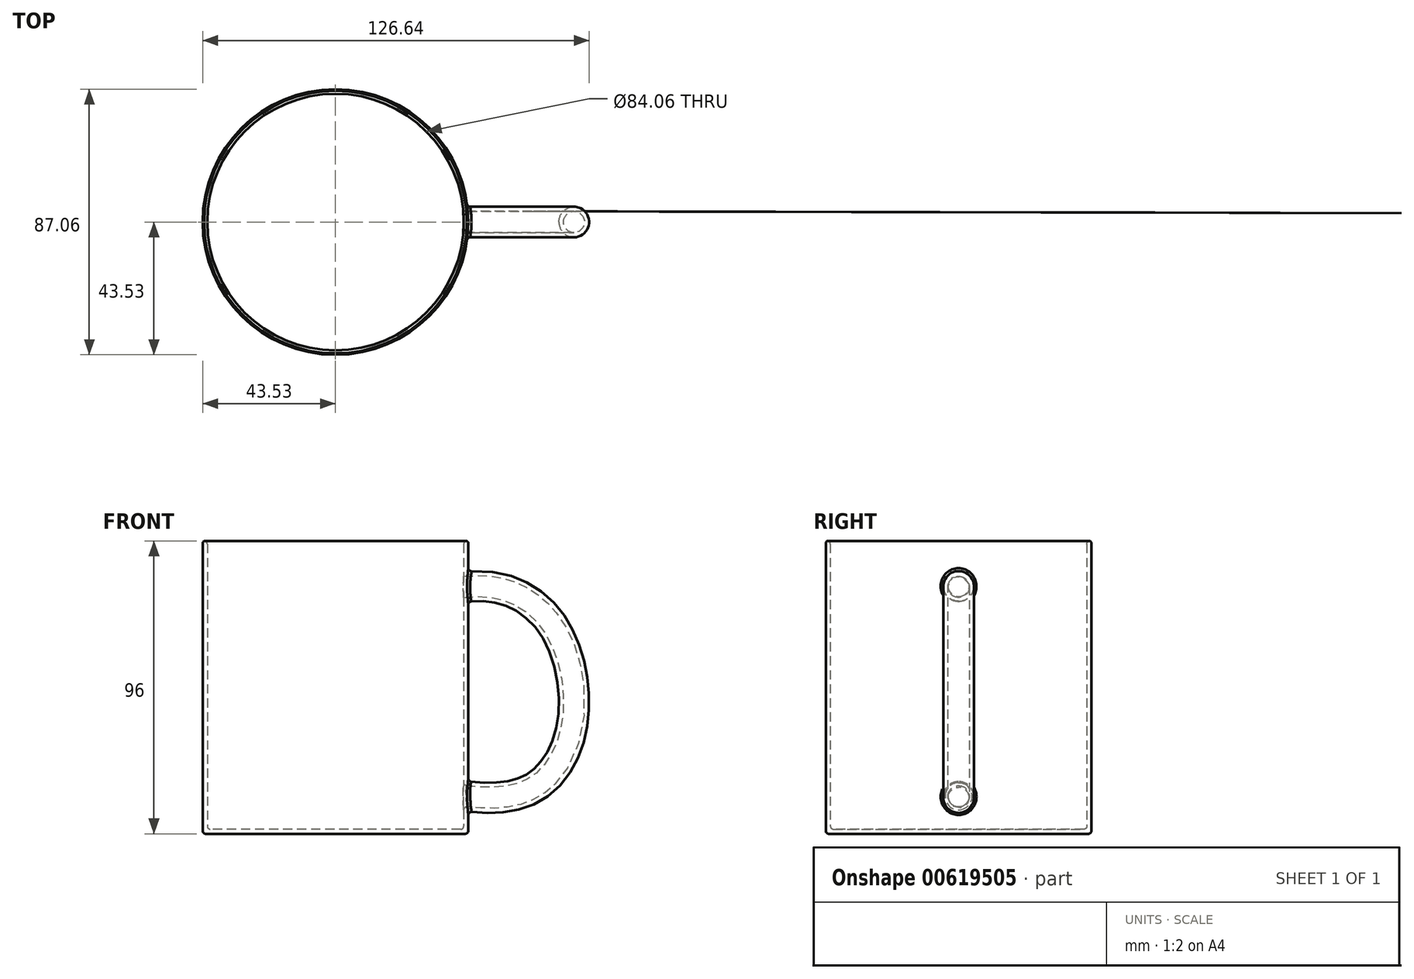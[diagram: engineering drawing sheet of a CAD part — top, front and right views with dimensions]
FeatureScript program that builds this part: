
annotation { "Feature Type Name" : "Feature", "Feature Type Description" : "" }
export const myFeature = defineFeature(function(context is Context, id is Id, definition is map)
    precondition{}
    {
        {
            var Q0;
            Q0=qCreatedBy(makeId("Top.planeOp"),FACE);
            var sketch = newSketch(context, id + "F0", { "sketchPlane" : qUnion([Q0])});
            skCircle(sketch, "E0", {"center": v(0, 0) * mm, "radius": 43.53 * mm});
            skSolve(sketch);
        }
        {
            var Q0;
            Q0 = qSketchRegion(id + "F0", true);
            extrude(context, id + "F1", {"entities" : qUnion([Q0]), "depth" : 96 * mm, "offsetDistance" : 25 * mm});
        }
        {
            var Q0;
            Q0=qCreatedBy(makeId("Front.planeOp"),FACE);
            var sketch = newSketch(context, id + "F2", { "sketchPlane" : qUnion([Q0])});
            skFitSpline(sketch, "E1", {"points": [v(33.38, 80.11) * mm, v(54.68, 80.88) * mm, v(72.35, 67.6) * mm, v(78.42, 37.38) * mm, v(68.76, 17.16) * mm, v(53.58, 11.3) * mm, v(33.56, 13.32) * mm], "startDerivative": vector(134.8, 28.45) * mm, "endDerivative": vector(-122.24, 25.91) * mm});
            skSolve(sketch);
        }
        {
            var Q0;
            Q0=qCreatedBy(makeId("Right.planeOp"),FACE);
            cPlane(context, id + "F3", {"entities" : qUnion([Q0]), "cplaneType" : CPlaneType.OFFSET, "offset" : 38.6 * mm, "width" : 150 * mm, "height" : 150 * mm});
        }
        {
            var Q0;
            Q0=qCreatedBy(id+"F3.planeOp",FACE);
            var sketch = newSketch(context, id + "F4", { "sketchPlane" : qUnion([Q0])});
            skCircle(sketch, "E2", {"center": v(0, 80.47) * mm, "radius": 5 * mm});
            skSolve(sketch);
        }
        {
            var Q0;
            Q0 = qSketchRegion(id + "F4", true);
            var Q1;
            Q1 = qConstructionFilter(qBodyType(qCreatedBy(id + "F2" ,EDGE), BodyType.WIRE), ConstructionObject.NO);
            sweep(context, id + "F5", {"operationType" : NewBodyOperationType.ADD, "profiles" : qUnion([Q0]), "path" : qUnion([Q1])});
        }
        {
            var Q0;
            Q0=makeQuery(id+"F1.opExtrude","CAP_FACE",FACE,{"disambiguationData":[OSD([sQuery(id+"F0.wireOp",EDGE,"E0")])],"isStart":false});
            shell(context, id + "F6", {"entities" : qUnion([Q0]), "thickness" : 1.5 * mm});
        }
        {
            var Q0;
            {var subQ0=sQuery(id+"F0.wireOp",EDGE,"E0");Q0=makeQuery(id+"F6.opShell","OFFSET_EDGE",EDGE,{"disambiguationData":[OSD([subQ0]),TDD([makeQuery(id+"F1.opExtrude","CAP_EDGE",EDGE,{"disambiguationData":[OSD([subQ0])],"isStart":false})])]});}
            fillet(context, id + "F7", {"entities" : qUnion([Q0]), "radius" : 1 * mm, "tangentPropagation" : true, "allowEdgeOverflow" : false});
        }
        {
            var Q0;
            Q0=makeQuery(id+"F1.opExtrude","CAP_EDGE",EDGE,{"disambiguationData":[OSD([sQuery(id+"F0.wireOp",EDGE,"E0")])],"isStart":false});
            fillet(context, id + "F8", {"entities" : qUnion([Q0]), "radius" : 1 * mm, "tangentPropagation" : true, "allowEdgeOverflow" : false});
        }
        {
            var Q0;
            Q0=makeQuery(id+"F1.opExtrude","CAP_FACE",FACE,{"disambiguationData":[OSD([sQuery(id+"F0.wireOp",EDGE,"E0")])],"isStart":true});
            fillet(context, id + "F9", {"entities" : qUnion([Q0]), "radius" : 1 * mm, "tangentPropagation" : true, "allowEdgeOverflow" : false});
        }
        {
            var Q0;
            {var subQ0=sQuery(id+"F0.wireOp",EDGE,"E0");Q0=makeQuery(id+"F6.opShell","OFFSET_EDGE",EDGE,{"disambiguationData":[OSD([subQ0]),TDD([makeQuery(id+"F1.opExtrude","CAP_EDGE",EDGE,{"disambiguationData":[OSD([subQ0])],"isStart":true})])]});}
            fillet(context, id + "F10", {"entities" : qUnion([Q0]), "radius" : 1 * mm, "tangentPropagation" : true, "allowEdgeOverflow" : false});
        }
        {
            var Q0;
            Q0=makeQuery(id+"F5.boolean.opBoolean","INTERSECT",EDGE,{"disambiguationData":[OD(1.0)],"derivedFrom":[makeQuery(id+"F1.opExtrude","SWEPT_FACE",FACE,{"disambiguationData":[OSD([sQuery(id+"F0.wireOp",EDGE,"E0")])]}),makeQuery(id+"F5.opSweep","SWEPT_FACE",FACE,{"disambiguationData":[OSD([sQuery(id+"F2.wireOp",EDGE,"E1"),sQuery(id+"F4.wireOp",EDGE,"E2")])]})]});
            fillet(context, id + "F11", {"entities" : qUnion([Q0]), "radius" : 1 * mm, "tangentPropagation" : true, "allowEdgeOverflow" : false});
        }
        {
            var Q0;
            Q0=makeQuery(id+"F5.boolean.opBoolean","INTERSECT",EDGE,{"disambiguationData":[OD(0.0)],"derivedFrom":[makeQuery(id+"F1.opExtrude","SWEPT_FACE",FACE,{"disambiguationData":[OSD([sQuery(id+"F0.wireOp",EDGE,"E0")])]}),makeQuery(id+"F5.opSweep","SWEPT_FACE",FACE,{"disambiguationData":[OSD([sQuery(id+"F2.wireOp",EDGE,"E1"),sQuery(id+"F4.wireOp",EDGE,"E2")])]})]});
            fillet(context, id + "F12", {"entities" : qUnion([Q0]), "radius" : 1 * mm, "tangentPropagation" : true, "allowEdgeOverflow" : false});
        }
        {
            var Q0;
            {var subQ0=sQuery(id+"F4.wireOp",EDGE,"E2");var subQ1=sQuery(id+"F2.wireOp",EDGE,"E1");var subQ2=sQuery(id+"F0.wireOp",EDGE,"E0");Q0=makeQuery(id+"F6.opShell","OFFSET_EDGE",EDGE,{"disambiguationData":[OSD([subQ2,subQ1,subQ0]),TDD([makeQuery(id+"F5.boolean.opBoolean","INTERSECT",EDGE,{"disambiguationData":[OD(0.0)],"derivedFrom":[makeQuery(id+"F1.opExtrude","SWEPT_FACE",FACE,{"disambiguationData":[OSD([subQ2])]}),makeQuery(id+"F5.opSweep","SWEPT_FACE",FACE,{"disambiguationData":[OSD([subQ1,subQ0])]})]})])]});}
            fillet(context, id + "F13", {"entities" : qUnion([Q0]), "radius" : 1 * mm, "tangentPropagation" : true, "allowEdgeOverflow" : false});
        }
    });
